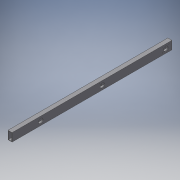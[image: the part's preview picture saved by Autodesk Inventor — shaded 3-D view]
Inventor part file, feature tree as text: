
AUTODESK INVENTOR PART (.ipt)
format: ipt  version: 2018 (Build 220112000, 112)  size: 186,368 bytes
history: native  units: in
note: dims shown in document units (in); Inventor stores cm internally (conversion verified against a paired STEP export)
features: extrude x8, sketch x8
ambient origin geometry x8: Origin, YZ Plane, XZ Plane, XY Plane, X Axis, Y Axis, Z Axis, Center Point
bodies: Solid1 (feature_tree)
feature tree (16):
  extrude  "Extrusion1"  Depth=2.0in
  extrude  "Extrusion2"  Depth=0.125in TaperAngle=0.0deg
  extrude  "Extrusion3"  Depth=0.5in TaperAngle=0.0deg
  extrude  "Extrusion4"  Depth=1.0in
  extrude  "Extrusion5"  Depth=1.0in TaperAngle=0.0deg
  extrude  "Extrusion7"  Depth=1.125in
  extrude  "Extrusion9"  Depth=1.0in
  extrude  "Extrusion10"  Depth=1.0in
  sketch  "Sketch1"  dims[d0=1.0in d1=2.0in]
  sketch  "Sketch2"  dims[d2=0.125in d3=38.5in d4=0.0in]
  sketch  "Sketch3"  dims[d5=1.0in d7=0.5in d8=0.0in]
  sketch  "Sketch4"  dims[d9=1.0in d10=7.0in]
  sketch  "Sketch5"  dims[d11=1.125in d12=1.0in d13=0.0in]
  sketch  "Sketch7"  dims[d14=22.0in d15=1.125in]
  sketch  "Sketch8"  dims[d16=1.0in d17=0.0in d18=1.0in]
  sketch  "Sketch9"  dims[d19=135.0deg d20=1.0in d21=0.16in d22=0.16in d23=1.0in d24=0.0in d34=1.0in d35=1.125in d36=0.5in d37=0.0in d45=0.9375in d46=0.2031in d47=0.2031in d48=0.2031in d49=0.2031in d50=1.0in d51=0.0in d52=0.125in d53=2.0in d54=1.0in d55=0.125in d56=0.125in d57=2.0in d58=1.0in d59=0.125in d60=0.5in d61=0.0in]
